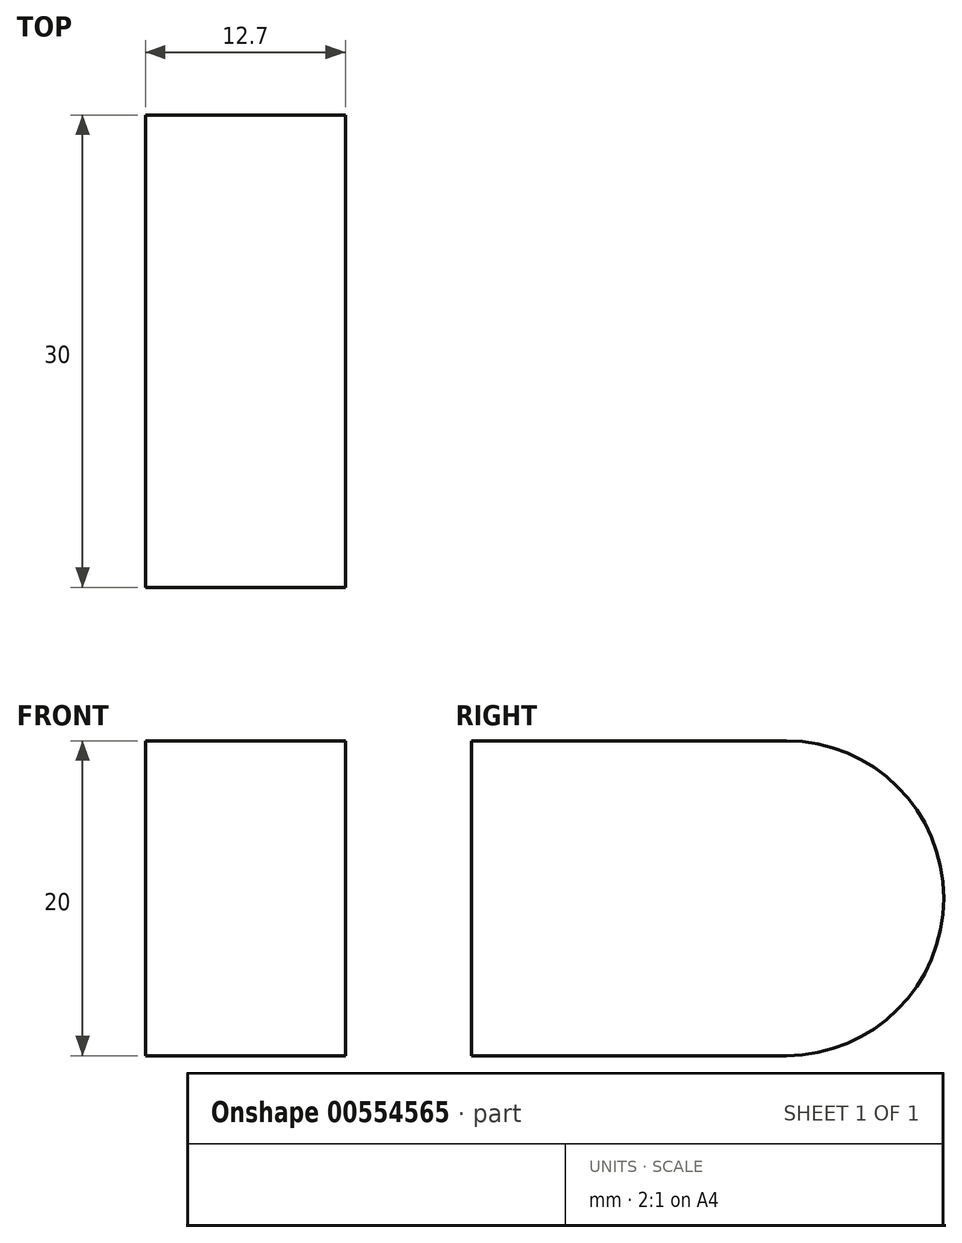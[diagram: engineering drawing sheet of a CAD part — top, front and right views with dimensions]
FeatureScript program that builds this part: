
annotation { "Feature Type Name" : "Feature", "Feature Type Description" : "" }
export const myFeature = defineFeature(function(context is Context, id is Id, definition is map)
    precondition{}
    {
        {
            var Q0;
            Q0=qCreatedBy(makeId("Right.planeOp"),FACE);
            var sketch = newSketch(context, id + "F0", { "sketchPlane" : qUnion([Q0])});
            skLineSegment(sketch, "E0.bottom", {"start": v(20.82, 6.63) * mm, "end": v(0.82, 6.63) * mm});
            skLineSegment(sketch, "E0.top", {"start": v(20.82, -13.37) * mm, "end": v(0.82, -13.37) * mm});
            skLineSegment(sketch, "E0.left", {"start": v(20.82, 6.63) * mm, "end": v(20.82, -13.37) * mm});
            skLineSegment(sketch, "E0.right", {"start": v(0.82, 6.63) * mm, "end": v(0.82, -13.37) * mm});
            skArc(sketch, "E1", {"start": v(20.82, -13.37) * mm, "mid": v(30.82, -3.37) * mm, "end": v(20.82, 6.63) * mm});
            skSolve(sketch);
        }
        {
            var Q0;
            Q0=makeQuery(id+"F0.imprint","IMPRINT",FACE,{"disambiguationData":[TD([[makeQuery(id+"F0.imprint","IMPRINT",EDGE,{"derivedFrom":sQuery(id+"F0.wireOp",EDGE,"E0.bottom")}),1.0]])]});
            var Q1;
            Q1=makeQuery(id+"F0.imprint","IMPRINT",FACE,{"disambiguationData":[TD([[makeQuery(id+"F0.imprint","IMPRINT",EDGE,{"derivedFrom":sQuery(id+"F0.wireOp",EDGE,"E0.left")}),1.0]])]});
            extrude(context, id + "F1", {"entities" : qUnion([Q0, Q1]), "depth" : 12.7 * mm, "offsetDistance" : 25.4 * mm});
        }
    });
